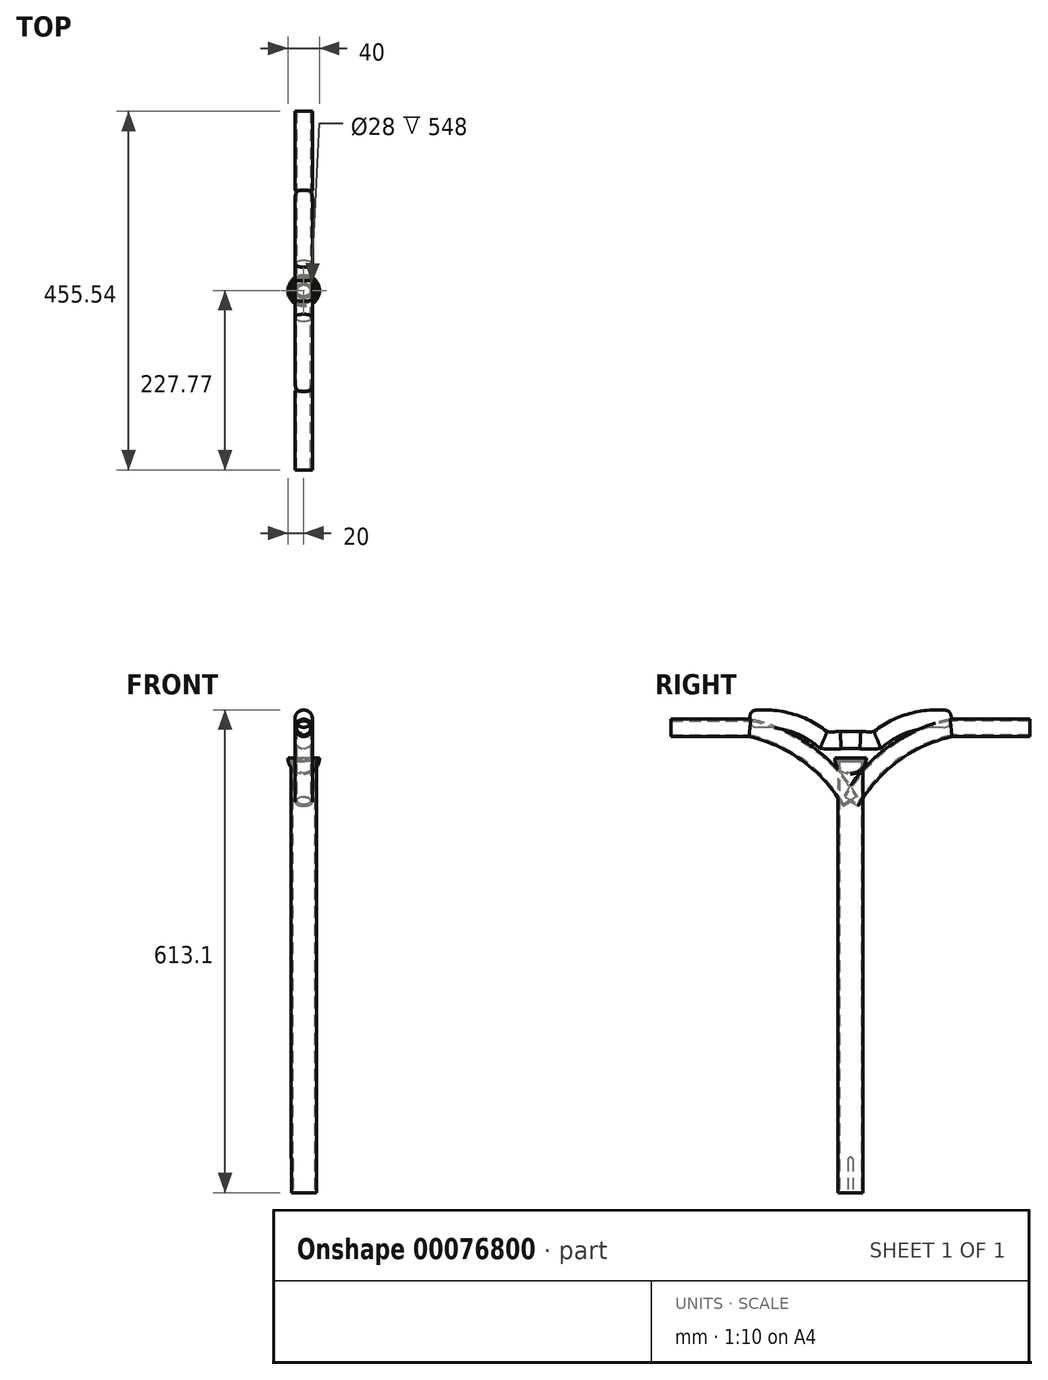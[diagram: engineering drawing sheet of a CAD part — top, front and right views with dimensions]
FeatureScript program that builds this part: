
annotation { "Feature Type Name" : "Feature", "Feature Type Description" : "" }
export const myFeature = defineFeature(function(context is Context, id is Id, definition is map)
    precondition{}
    {
        {
            var Q0;
            Q0=qCreatedBy(makeId("Top.planeOp"),FACE);
            var sketch = newSketch(context, id + "F0", { "sketchPlane" : qUnion([Q0])});
            skCircle(sketch, "E0", {"center": v(0, 0) * mm, "radius": 16 * mm});
            skSolve(sketch);
        }
        {
            var Q0;
            Q0 = qSketchRegion(id + "F0", true);
            extrude(context, id + "F1", {"entities" : qUnion([Q0]), "depth" : 550 * mm});
        }
        {
            var Q0;
            Q0=makeQuery(id+"F1.opExtrude","CAP_FACE",FACE,{"disambiguationData":[OSD([sQuery(id+"F0.wireOp",EDGE,"E0")])],"isStart":true});
            shell(context, id + "F2", {"entities" : qUnion([Q0]), "thickness" : 2 * mm});
        }
        {
            var Q0;
            Q0=qCreatedBy(makeId("Right.planeOp"),FACE);
            var sketch = newSketch(context, id + "F3", { "sketchPlane" : qUnion([Q0])});
            skLineSegment(sketch, "E1.bottom", {"start": v(3, 0) * mm, "end": v(-3, 0) * mm});
            skLineSegment(sketch, "E1.top", {"start": v(0, 45) * mm, "end": v(0, 45) * mm});
            skLineSegment(sketch, "E1.left", {"start": v(3, 0) * mm, "end": v(3, 42) * mm});
            skLineSegment(sketch, "E1.right", {"start": v(-3, 0) * mm, "end": v(-3, 42) * mm});
            skPoint(sketch, "E2", {"position": v(0, 45) * mm});
            skPoint(sketch, "E3.visualSharp", {"position": v(3, 45) * mm});
            skArc(sketch, "E3.filletArc", {"start": v(3, 42) * mm, "mid": v(2.12, 44.12) * mm, "end": v(0, 45) * mm});
            skPoint(sketch, "E4.visualSharp", {"position": v(-3, 45) * mm});
            skArc(sketch, "E4.filletArc", {"start": v(0, 45) * mm, "mid": v(-2.12, 44.12) * mm, "end": v(-3, 42) * mm});
            skSolve(sketch);
        }
        {
            var Q0;
            Q0 = qSketchRegion(id + "F3", true);
            extrude(context, id + "F4", {"entities" : qUnion([Q0]), "operationType" : NewBodyOperationType.REMOVE, "endBound" : BoundingType.THROUGH_ALL, "oppositeDirection" : true, "depth" : 25 * mm});
        }
        {
            var Q0;
            Q0=qCreatedBy(makeId("Right.planeOp"),FACE);
            var sketch = newSketch(context, id + "F5", { "sketchPlane" : qUnion([Q0])});
            skArc(sketch, "E5", {"start": v(127.77, 590.48) * mm, "mid": v(53.89, 557.03) * mm, "end": v(0, 496.4) * mm});
            skLineSegment(sketch, "E6", {"start": v(127.77, 590.48) * mm, "end": v(227.77, 590.48) * mm});
            skSolve(sketch);
        }
        {
            var Q0;
            Q0=sQuery(id+"F5.wireOp",VERTEX,"E6.end");
            var Q1;
            Q1=qCreatedBy(makeId("Front.planeOp"),FACE);
            cPlane(context, id + "F6", {"entities" : qUnion([Q0, Q1]), "cplaneType" : CPlaneType.PLANE_POINT, "offset" : 150 * mm, "width" : 150 * mm, "height" : 150 * mm});
        }
        {
            var Q0;
            Q0=qCreatedBy(id+"F6.planeOp",FACE);
            var sketch = newSketch(context, id + "F7", { "sketchPlane" : qUnion([Q0])});
            skCircle(sketch, "E7", {"center": v(0, 590.48) * mm, "radius": 11 * mm});
            skSolve(sketch);
        }
        {
            var Q0;
            Q0 = qSketchRegion(id + "F7", true);
            var Q1;
            Q1 = qConstructionFilter(qBodyType(qCreatedBy(id + "F5" ,EDGE), BodyType.WIRE), ConstructionObject.NO);
            sweep(context, id + "F8", {"profiles" : qUnion([Q0]), "path" : qUnion([Q1])});
        }
        {
            var Q0;
            Q0=makeQuery(id+"F8.opSweep","CAP_FACE",FACE,{"disambiguationData":[OSD([sQuery(id+"F5.wireOp",VERTEX,"E6.end"),sQuery(id+"F7.wireOp",EDGE,"E7")])],"isStart":true});
            shell(context, id + "F9", {"entities" : qUnion([Q0]), "thickness" : 2 * mm});
        }
        {
            var Q0;
            Q0=makeQuery(id+"F8.opSweep","SWEPT_BODY",BODY,{"disambiguationData":[OSD([sQuery(id+"F5.wireOp",EDGE,"E6"),sQuery(id+"F7.wireOp",EDGE,"E7")])]});
            var Q1;
            Q1=qCreatedBy(makeId("Front.planeOp"),FACE);
            mirror(context, id + "F10", {"entities" : qUnion([Q0]), "mirrorPlane" : qUnion([Q1])});
        }
        {
            var Q0;
            Q0=qCreatedBy(makeId("Right.planeOp"),FACE);
            var sketch = newSketch(context, id + "F11", { "sketchPlane" : qUnion([Q0])});
            skLineSegment(sketch, "E8", {"start": v(-128, 602.1) * mm, "end": v(-108, 602.1) * mm});
            skArc(sketch, "E9", {"start": v(-34.22, 575) * mm, "mid": v(-68.7, 595.11) * mm, "end": v(-108, 602.1) * mm});
            skArc(sketch, "E10", {"start": v(-34.22, 575) * mm, "mid": v(-23.36, 574.47) * mm, "end": v(-12.5, 575) * mm});
            skLineSegment(sketch, "E11", {"start": v(-12.5, 575) * mm, "end": v(0, 575) * mm});
            skLineSegment(sketch, "E12", {"start": v(0, 0) * mm, "end": v(0, 576.94) * mm, "construction": true});
            skLineSegment(sketch, "E13.MirrorCS", {"start": v(128, 602.1) * mm, "end": v(108, 602.1) * mm});
            skArc(sketch, "E14.MirrorCS", {"start": v(34.22, 575) * mm, "mid": v(68.7, 595.11) * mm, "end": v(108, 602.1) * mm});
            skArc(sketch, "E15.MirrorCS", {"start": v(34.22, 575) * mm, "mid": v(23.36, 574.47) * mm, "end": v(12.5, 575) * mm});
            skLineSegment(sketch, "E16.MirrorCS", {"start": v(12.5, 575) * mm, "end": v(0, 575) * mm});
            skSolve(sketch);
        }
        {
            var Q0;
            Q0=sQuery(id+"F11.wireOp",VERTEX,"E13.MirrorCS.start");
            var Q1;
            Q1=qCreatedBy(id+"F6.planeOp",FACE);
            cPlane(context, id + "F12", {"entities" : qUnion([Q0, Q1]), "cplaneType" : CPlaneType.PLANE_POINT, "offset" : 150 * mm, "width" : 150 * mm, "height" : 150 * mm});
        }
        {
            var Q0;
            Q0=qCreatedBy(id+"F12.planeOp",FACE);
            var sketch = newSketch(context, id + "F13", { "sketchPlane" : qUnion([Q0])});
            skCircle(sketch, "E17", {"center": v(0, 602.1) * mm, "radius": 11 * mm});
            skSolve(sketch);
        }
        {
            var Q0;
            Q0 = qSketchRegion(id + "F13", true);
            var Q1;
            Q1=sQuery(id+"F11.wireOp",EDGE,"E8");
            var Q2;
            Q2=sQuery(id+"F11.wireOp",EDGE,"E9");
            var Q3;
            Q3=sQuery(id+"F11.wireOp",EDGE,"E10");
            var Q4;
            Q4=sQuery(id+"F11.wireOp",EDGE,"E11");
            var Q5;
            Q5=sQuery(id+"F11.wireOp",EDGE,"E16.MirrorCS");
            var Q6;
            Q6=sQuery(id+"F11.wireOp",EDGE,"E15.MirrorCS");
            var Q7;
            Q7=sQuery(id+"F11.wireOp",EDGE,"E14.MirrorCS");
            var Q8;
            Q8=sQuery(id+"F11.wireOp",EDGE,"E13.MirrorCS");
            sweep(context, id + "F14", {"profiles" : qUnion([Q0]), "path" : qUnion([Q1, Q2, Q3, Q4, Q5, Q6, Q7, Q8])});
        }
        {
            var Q0;
            {var subQ0=sQuery(id+"F13.wireOp",EDGE,"E17");var subQ1=sQuery(id+"F11.wireOp",VERTEX,"E13.MirrorCS.start");Q0=makeQuery(id+"F14.boolean.opBoolean","SPLIT",EDGE,{"disambiguationData":[TD([makeQuery(id+"F8.opSweep","SWEPT_FACE",FACE,{"disambiguationData":[OSD([sQuery(id+"F5.wireOp",EDGE,"E6"),sQuery(id+"F7.wireOp",EDGE,"E7")])]})])],"derivedFrom":makeQuery(id+"F14.opSweep","CAP_EDGE",EDGE,{"disambiguationData":[OSD([subQ1,subQ0])],"isStart":true})});}
            var Q1;
            {var subQ0=sQuery(id+"F13.wireOp",EDGE,"E17");var subQ1=sQuery(id+"F11.wireOp",VERTEX,"E8.start");Q1=makeQuery(id+"F14.boolean.opBoolean","SPLIT",EDGE,{"disambiguationData":[TD([makeQuery(id+"F10.opPattern","COPY",FACE,{"derivedFrom":makeQuery(id+"F8.opSweep","SWEPT_FACE",FACE,{"disambiguationData":[OSD([sQuery(id+"F5.wireOp",EDGE,"E6"),sQuery(id+"F7.wireOp",EDGE,"E7")])]}),"instanceName":"1"})])],"derivedFrom":makeQuery(id+"F14.opSweep","CAP_EDGE",EDGE,{"disambiguationData":[OSD([subQ1,subQ0])],"isStart":false})});}
            fillet(context, id + "F15", {"entities" : qUnion([Q0, Q1]), "radius" : 10 * mm, "tangentPropagation" : true, "rho" : 0.5, "crossSection" : FilletCrossSection.CONIC, "allowEdgeOverflow" : false});
        }
        {
            var Q0;
            Q0=qCreatedBy(makeId("Right.planeOp"),FACE);
            var sketch = newSketch(context, id + "F16", { "sketchPlane" : qUnion([Q0])});
            skArc(sketch, "E18", {"start": v(0, 532) * mm, "mid": v(14.14, 537.86) * mm, "end": v(20, 552) * mm});
            skLineSegment(sketch, "E19", {"start": v(0, 532) * mm, "end": v(0, 552) * mm});
            skLineSegment(sketch, "E20", {"start": v(20, 552) * mm, "end": v(0, 552) * mm});
            skSolve(sketch);
        }
        {
            var Q0;
            Q0=makeQuery(id+"F16.imprint","IMPRINT",FACE,{"disambiguationData":[TD([[makeQuery(id+"F16.imprint","IMPRINT",EDGE,{"derivedFrom":sQuery(id+"F16.wireOp",EDGE,"E18")}),1.0]])]});
            var Q1;
            Q1=sQuery(id+"F16.wireOp",EDGE,"E19");
            revolve(context, id + "F17", {"entities" : qUnion([Q0]), "axis" : qUnion([Q1]), "revolveType" : RevolveType.FULL});
        }
        {
            var Q0;
            Q0=makeQuery(id+"F17.opRevolve","SWEPT_FACE",FACE,{"disambiguationData":[OSD([sQuery(id+"F16.wireOp",EDGE,"E20")])]});
            shell(context, id + "F18", {"entities" : qUnion([Q0]), "thickness" : 2 * mm});
        }
    });
